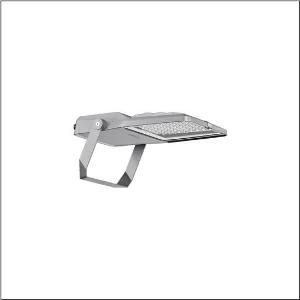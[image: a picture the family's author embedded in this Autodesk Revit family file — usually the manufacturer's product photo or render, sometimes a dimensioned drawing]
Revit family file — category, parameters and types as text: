
# Revit family: floodlight_fl_21_iq_mini___pl33t_5xa7772d1f1a_784a
name_source: partatom
category: Lighting Fixtures
units: mm (PartAtom-declared; Revit-internal decimal feet)

## family parameters
Cut with Voids When Loaded = No
Host = Face
Light Source = No
Part Type = Normal
Room Calculation Point = No
Round Connector Dimension = Use Diameter
Shared = No

## types (1)
- --- (1 x LED, 14590 lm, 143 W, 2200K)
    Apparent Load = 143 VA
    CIE Flux Codes = 26 75 99 100 100
    Color Rendering = 70
    Color Temperature = 2200K
    Default Elevation = 1800 mm
    Description = Floodlight FL 21 iQ mini, floodlight, primary light control with lens, of PMMA, primary optical cover: protective disc, of toughened safety glass, transparent, light distribution: PL33T, light emission: direct distribution, installation type: surface-mounted, LED, High Power LED, rated luminous flux: 14.590lm, luminous efficacy: 102lm/W, light colour: 722, colour temperature: 2200K, control: Street-Remote, Auto-Match, Temp-Guard, Night-Set, Smart-Wire, Desk-Remote (wireless, voltage-free reading and setting of iQ features in the workshop via application-optimized NFC function/RFID function), optimised constant luminous flux control (CLO 2.0), with terminal, 6-pole, mains connection: 220..240V, AC, 50/60Hz, start of lifetime: 143W, end of service life: 152W, reduction: 61W, luminaire housing, of diecast aluminium, powder-coated, Siteco® metallic grey (DB 702S), corrosivity category C5 mid according to DIN EN ISO 12944, sealing non-destructively replaceable, mounting bracket, of steel, galvanised, powder-coated, Siteco® metallic grey (DB 702S), protection rating (complete): IP66, insulation class (complete): insulation class II (safety insulation), certification: CE, ENEC, VDE, protection symbol: D, impact resistance: IK08, permissible operating ambient temperature: -40..+40°C, permissible operating ambient temperature for outdoor applications: -40..+50°C, standard: DIN EN 12944, LABS conformity tested according to VDMA 24364:2018-05, packaging unit: 1 piece

Light Distribution: PL33T
    Height = 70 mm
    Lamp = 1 x LED
    Lamp Light Flux = 14590 lm
    Lamp Power = 143 W
    Lamp count = 1
    Length = 485 mm
    Luminous efficacy = 102 lm/W
    Manufacturer = Siteco
    ModVariant = No
    Model = 5XA7772D1F1A
    Number of Poles = 1
    OnlyDefault = Yes
    Power Factor = 1
    Product Name = Floodlight FL 21 iQ mini | PL33T
    Product group = floodlight | pylon annexe
    ProductGroupID = 6200
    Protection Class = Protection class II
    Protection Degree = IP 66
    RLX_Detail_Level = 1
    RLX_Emergency_Light_Flux = 0 lm
    RLX_Emergency_Type = 0
    RLX_Emergency_Type_DB = No
    RlxData = <blob elided: 96285 chars, md5=acf34643>
    Socket = socket
    Standby Power = 0 W
    System Light Flux = 14590 lm
    System Power = 143 W
    Type Comments = factory setting: luminous flux: 100 % | dim-lin: 254 | 730 mA
    Type Image = l_1006845.jpg
    URL = http://relux.com
    VarID = @adj_081529
    Voltage = 0 V
    Weight = 0.00 kg
    Width = 337 mm

## geometry (parser evidence)
native form markers: Blend x4, Sweep x15
no freeform markers — native parametric forms only
